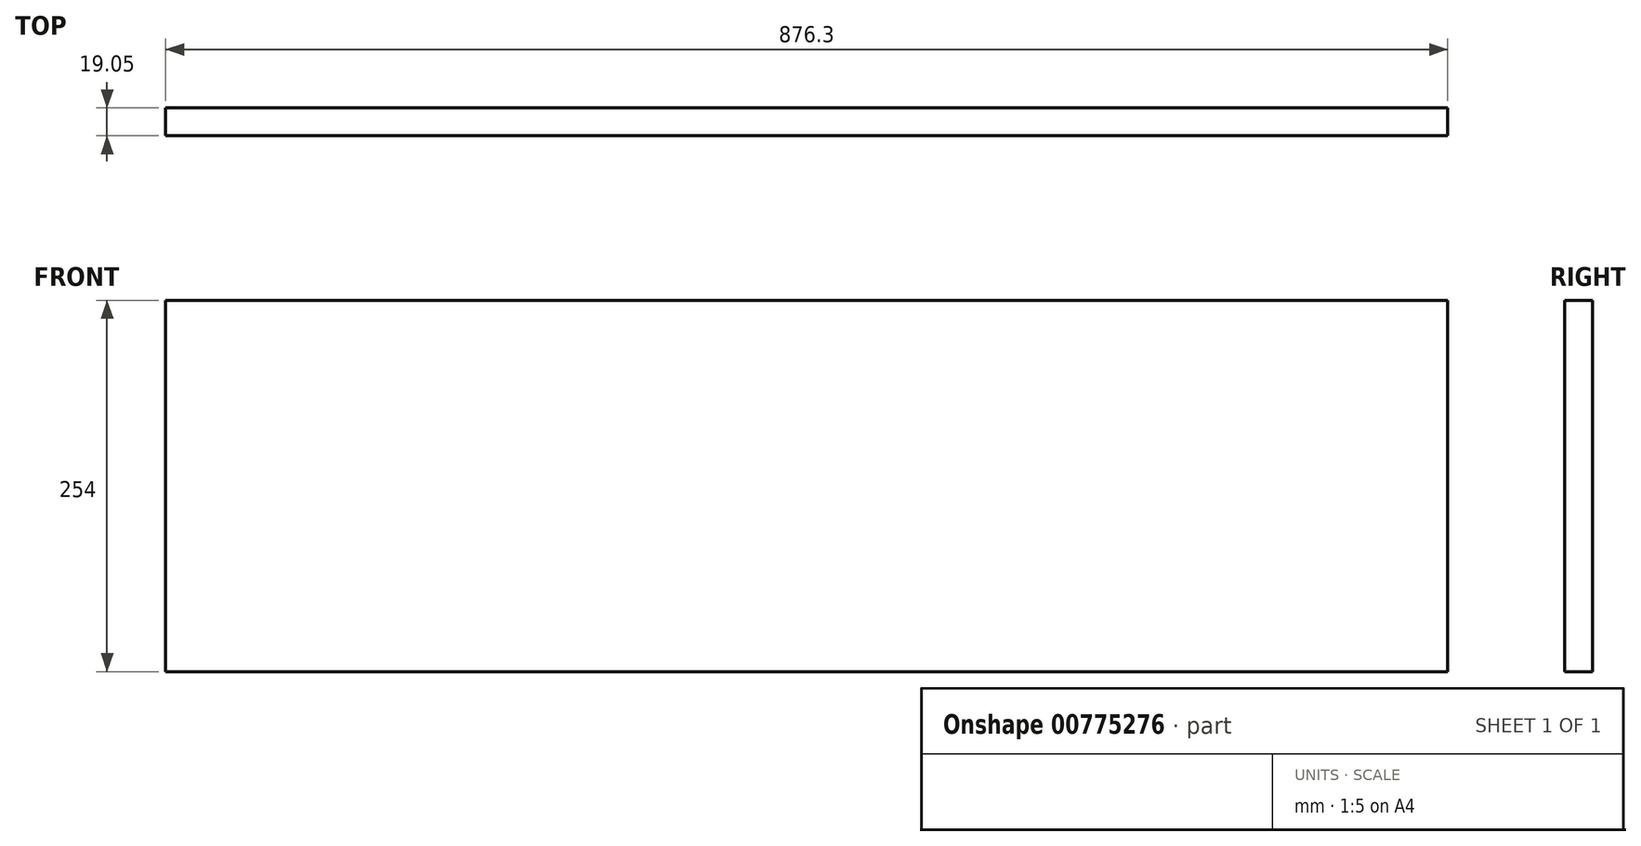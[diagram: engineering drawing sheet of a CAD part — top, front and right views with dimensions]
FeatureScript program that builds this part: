
annotation { "Feature Type Name" : "Feature", "Feature Type Description" : "" }
export const myFeature = defineFeature(function(context is Context, id is Id, definition is map)
    precondition{}
    {
        {
            var Q0;
            Q0=qCreatedBy(makeId("Front.planeOp"),FACE);
            var sketch = newSketch(context, id + "F0", { "sketchPlane" : qUnion([Q0])});
            skLineSegment(sketch, "E0.bottom", {"start": v(0, 0) * mm, "end": v(-876.3, 0) * mm});
            skLineSegment(sketch, "E0.top", {"start": v(0, 254) * mm, "end": v(-876.3, 254) * mm});
            skLineSegment(sketch, "E0.left", {"start": v(0, 0) * mm, "end": v(0, 254) * mm});
            skLineSegment(sketch, "E0.right", {"start": v(-876.3, 0) * mm, "end": v(-876.3, 254) * mm});
            skSolve(sketch);
        }
        {
            var Q0;
            Q0 = qSketchRegion(id + "F0", true);
            extrude(context, id + "F1", {"entities" : qUnion([Q0]), "depth" : 19.05 * mm, "offsetDistance" : 25.4 * mm});
        }
    });
